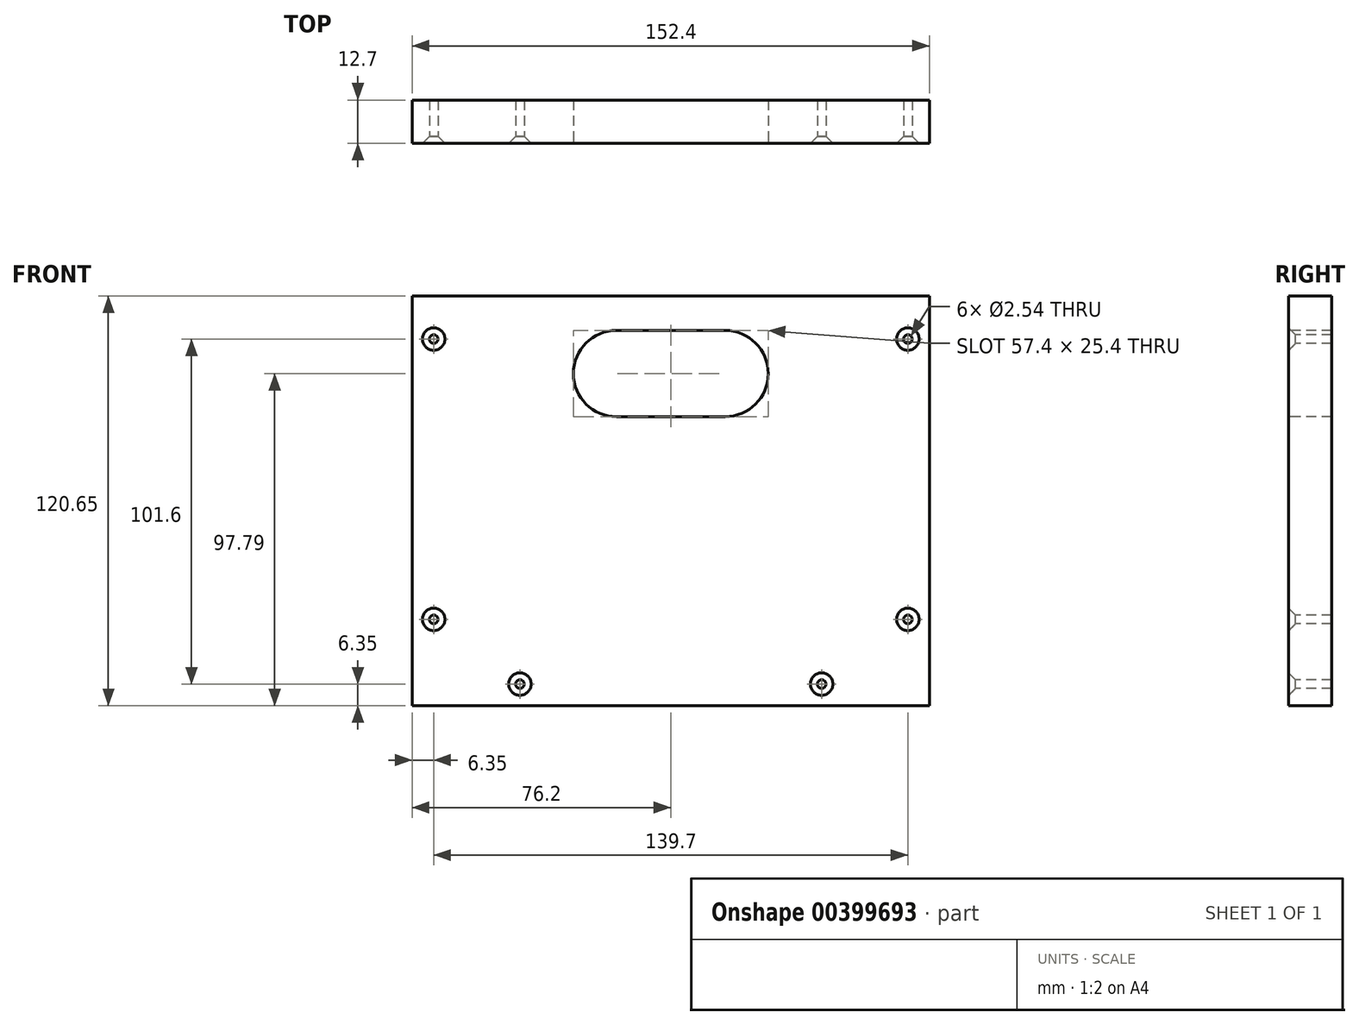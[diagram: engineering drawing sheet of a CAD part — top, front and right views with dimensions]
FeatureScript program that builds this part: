
annotation { "Feature Type Name" : "Feature", "Feature Type Description" : "" }
export const myFeature = defineFeature(function(context is Context, id is Id, definition is map)
    precondition{}
    {
        {
            var Q0;
            Q0=qCreatedBy(makeId("Front.planeOp"),FACE);
            var sketch = newSketch(context, id + "F0", { "sketchPlane" : qUnion([Q0])});
            skLineSegment(sketch, "E0.bottom", {"start": v(-76.2, 63.5) * mm, "end": v(76.2, 63.5) * mm});
            skLineSegment(sketch, "E0.top", {"start": v(-76.2, -57.15) * mm, "end": v(76.2, -57.15) * mm});
            skLineSegment(sketch, "E0.left", {"start": v(-76.2, 63.5) * mm, "end": v(-76.2, -57.15) * mm});
            skLineSegment(sketch, "E0.right", {"start": v(76.2, 63.5) * mm, "end": v(76.2, -57.15) * mm});
            skSolve(sketch);
        }
        {
            var Q0;
            Q0=makeQuery(id+"F0.imprint","IMPRINT",FACE,{"disambiguationData":[TD([[makeQuery(id+"F0.imprint","IMPRINT",EDGE,{"derivedFrom":sQuery(id+"F0.wireOp",EDGE,"E0.bottom")}),-1.0]])]});
            extrude(context, id + "F1", {"entities" : qUnion([Q0]), "depth" : 12.7 * mm});
        }
        {
            var Q0;
            Q0=makeQuery(id+"F1.opExtrude","CAP_FACE",FACE,{"disambiguationData":[OSD([sQuery(id+"F0.wireOp",EDGE,"E0.bottom"),sQuery(id+"F0.wireOp",EDGE,"E0.top"),sQuery(id+"F0.wireOp",EDGE,"E0.left"),sQuery(id+"F0.wireOp",EDGE,"E0.right")])],"isStart":false});
            var sketch = newSketch(context, id + "F2", { "sketchPlane" : qUnion([Q0])});
            skLineSegment(sketch, "E1", {"start": v(-69.85, 63.5) * mm, "end": v(-69.85, -57.15) * mm, "construction": true});
            skLineSegment(sketch, "E2", {"start": v(-76.2, -50.8) * mm, "end": v(76.2, -50.8) * mm, "construction": true});
            skLineSegment(sketch, "E3", {"start": v(0, 0) * mm, "end": v(0, 63.5) * mm, "construction": true});
            skLineSegment(sketch, "E4.MirrorCS", {"start": v(69.85, 63.5) * mm, "end": v(69.85, -57.15) * mm, "construction": true});
            skPoint(sketch, "E5", {"position": v(-69.85, 50.8) * mm});
            skPoint(sketch, "E6", {"position": v(-69.85, -31.75) * mm});
            skPoint(sketch, "E7", {"position": v(-44.45, -50.8) * mm});
            skPoint(sketch, "E8.MirrorP", {"position": v(69.85, 50.8) * mm});
            skPoint(sketch, "E9.MirrorP", {"position": v(69.85, -31.75) * mm});
            skPoint(sketch, "E10.MirrorP", {"position": v(44.45, -50.8) * mm});
            skSolve(sketch);
        }
        {
            var Q0;
            Q0=sQuery(id+"F2.wireOp",VERTEX,"E5");
            var Q1;
            Q1=sQuery(id+"F2.wireOp",VERTEX,"E6");
            var Q2;
            Q2=sQuery(id+"F2.wireOp",VERTEX,"E7");
            var Q3;
            Q3=sQuery(id+"F2.wireOp",VERTEX,"E10.MirrorP");
            var Q4;
            Q4=sQuery(id+"F2.wireOp",VERTEX,"E9.MirrorP");
            var Q5;
            Q5=sQuery(id+"F2.wireOp",VERTEX,"E8.MirrorP");
            var Q6;
            Q6=makeQuery(id+"F1.opExtrude","SWEPT_BODY",BODY,{"disambiguationData":[OSD([sQuery(id+"F0.wireOp",EDGE,"E0.bottom"),sQuery(id+"F0.wireOp",EDGE,"E0.top"),sQuery(id+"F0.wireOp",EDGE,"E0.left"),sQuery(id+"F0.wireOp",EDGE,"E0.right")])]});
            hole(context, id + "F3", {"style" : HoleStyle.C_SINK, "endStyle" : HoleEndStyle.THROUGH, "holeDiameter" : 2.54 * mm, "cSinkDiameter" : 6.6 * mm, "cSinkAngle" : 90 * degree, "isTappedThrough" : true, "tappedDepth" : 12.7 * mm, "tapClearance" : 3, "locations" : qUnion([Q0, Q1, Q2, Q3, Q4, Q5]), "scope" : qUnion([Q6])});
        }
        {
            var Q0;
            Q0=makeQuery(id+"F1.opExtrude","CAP_FACE",FACE,{"disambiguationData":[OSD([sQuery(id+"F0.wireOp",EDGE,"E0.bottom"),sQuery(id+"F0.wireOp",EDGE,"E0.top"),sQuery(id+"F0.wireOp",EDGE,"E0.left"),sQuery(id+"F0.wireOp",EDGE,"E0.right")])],"isStart":false});
            var sketch = newSketch(context, id + "F4", { "sketchPlane" : qUnion([Q0])});
            skLineSegment(sketch, "E11", {"start": v(0, 0) * mm, "end": v(0, 63.5) * mm, "construction": true});
            skLineSegment(sketch, "E12", {"start": v(-52.5, 40.64) * mm, "end": v(49.7, 40.64) * mm, "construction": true});
            skLineSegment(sketch, "E13", {"start": v(-16, 53.34) * mm, "end": v(0, 53.34) * mm});
            skArc(sketch, "E14", {"start": v(-16, 53.34) * mm, "mid": v(-28.7, 40.64) * mm, "end": v(-16, 27.94) * mm});
            skLineSegment(sketch, "E15.MirrorCS", {"start": v(-16, 27.94) * mm, "end": v(0, 27.94) * mm});
            skLineSegment(sketch, "E16.MirrorCS", {"start": v(16, 53.34) * mm, "end": v(0, 53.34) * mm});
            skArc(sketch, "E17.MirrorCS", {"start": v(16, 53.34) * mm, "mid": v(28.7, 40.64) * mm, "end": v(16, 27.94) * mm});
            skLineSegment(sketch, "E18.MirrorCS", {"start": v(16, 27.94) * mm, "end": v(0, 27.94) * mm});
            skSolve(sketch);
        }
        {
            var Q0;
            Q0=makeQuery(id+"F4.imprint","IMPRINT",FACE,{"disambiguationData":[TD([[makeQuery(id+"F4.imprint","IMPRINT",EDGE,{"derivedFrom":sQuery(id+"F4.wireOp",EDGE,"E13")}),-1.0]])]});
            extrude(context, id + "F5", {"entities" : qUnion([Q0]), "operationType" : NewBodyOperationType.REMOVE, "endBound" : BoundingType.THROUGH_ALL, "oppositeDirection" : true, "depth" : 25.4 * mm});
        }
    });
